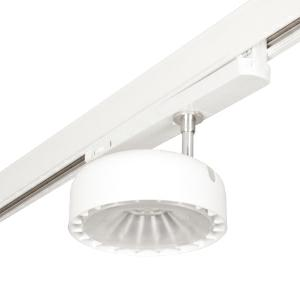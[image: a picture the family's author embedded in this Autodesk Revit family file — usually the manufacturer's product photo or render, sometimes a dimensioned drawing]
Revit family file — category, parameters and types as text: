
# Revit family: 3f_filippi_-_3f_emilio_track_ellittico_3f_filippi_-_47622_-_3f_emilio_tk_led_4000-830_ell
name_source: partatom
category: Lighting Fixtures
units: mm (PartAtom-declared; Revit-internal decimal feet)

## family parameters
Cut with Voids When Loaded = No
Host = Face
Light Source = No
Part Type = Normal
Room Calculation Point = No
Round Connector Dimension = Use Diameter
Shared = No

## types (1)
- 3F Filippi - 3F Emilio Track Ellittico (1 x LED, 3927 lm, 34 W, 3000 K)
    Apparent Load = 34 VA
    Approval mark = CE
    CIE Flux Codes = 84 95 99 100 100
    Color Rendering = 80
    Color Temperature = 3000 K
    Control Gear = Electronic ballast
    Default Elevation = 1800 mm
    Description = Adjustable spot light with minimal dimensions for accent lighting, to be integrated into the busbar.

ILLUMINOTECHNICAL
Luminous efficiency 100% (DLOR 100%, ULOR 0%).
Initial luminous flux of the luminaire 3927 lm.
Symmetrical and elliptical distribution.
Tabular UGR (CIE 117 - 4H-8H; S=0.25H; 70/50/20): RUG 22.4 - 26.8.
Beam angle: 46° - 89°.
Luminous efficacy 116 lm/W.
Lifetime (L90/B20): 30000 h. (tq+25°C)
Lifetime (L80/B20): 50000 h. (tq+25°C)
Sudden decreased luminous flux after 50000 hours: 0% (C0).
Photobiological safety in compliance with IEC/TR 62778: RG1 low risk, (IEC 62471).
In compliance with IEC/EN 62722-2-1 - IEC/EN 62717 standards.

SOURCE
Compact LED module 4000/830.
Energy efficiency class (UE 2019/2020 - UE 2019/2015): E.
CIE 13.3 Colour rendering index: CRI >80 (R9 <50%).
IES TM-30 Fidelity Index: Rf = 84 Rg = 95.
CCT nominal colour temperature 3000 K.
Colour initial tolerance (MacAdam): SDCM 3.
Zhaga Book 3 compliant.

MECHANICAL
Wired unit in white polycarbonate with busbar adaptor.
Single-piece in die-cast aluminium with passive dissipation, white colour, with perimeter cooling slots on upper edge, giving a crown of light effect to the fitting.
Invisible lock for positioning the luminous flux.
Lens made from transparent methacrylate (PMMA) with glossy surface and differentiated photo-etched.
Positioning arm in galvanised brass with sphere to allow for vertical positioning at angles from 0° to 90° and horizontal positioning from 0° to 290°.
Dimensions: diameter 130 mm, length 230 mm, height 105 mm. Weight 0.825 kg.
IP20 protection degree.
Glow-wire test resistance 650°C.

ELECTRICAL
Wiring unit separate from the body, invisible and integrated into the busbar.
Halogen Free electronic wiring 230V-50/60Hz, power factor 0.95, THD <25%, constant output current, SELV, class II, 1 driver.
Power of the luminaire 34 W.
ENEC - CE.
SAFE FLICKER: PstLM=<1 and SVM=<0.4 (IEC TR 61547-1 and IEC TR 63158), to ensure a more comfortable and safe light.
Ambient temperature from 0°C to +25°C.
Temperature class T6 max 85°C.
Relative humidity UR: <85%.

INSTALLATION
Track.

APPLICATIONS
Transit areas, spotlighting in commercial environments, exhibition areas, restaurants, shops and shop windows.

WARNING
Luminaire designed for disposal/recycling at end-of-life.
Replaceable (LED only) light source by a professional. Replaceable control gear by a professional.
    Height = 105 mm
    Lamp = 1 x LED
    Lamp Light Flux = 3927 lm
    Lamp Power = 34 W
    Lamp count = 1
    Length = 230 mm
    Lifetime = 50000 h
    Luminous efficacy = 116 lm/W
    Manufacturer = 3F Filippi
    ModVariant = No
    Model = 3F Filippi - 47622 - 3F Emilio TK LED 4000-830 ELL
    Mounting Place = Ceiling
    Mounting Type = Rail mounted
    Number of Poles = 1
    OnlyDefault = Yes
    Power Factor = 1
    Product Name = 3F Filippi - 3F Emilio Track Ellittico
    Product group = track mounted spotlight
    ProductGroupID = 12
    Protection Class = Protection class II
    Protection Degree = IP 20
    RLX_Detail_Level = 1
    RLX_Emergency_Light_Flux = 0 lm
    RLX_Emergency_Type = 0
    RLX_Emergency_Type_DB = No
    RlxData = <blob elided: 152337 chars, md5=ca9f1d0e>
    Socket = socket
    Standby Power = 0 W
    System Light Flux = 3927 lm
    System Power = 34 W
    Type Comments = Product without accessories
    Type Image = 3ffilippi_47622.jpg
    URL = http://relux.com
    VarID = ---
    Voltage = 0 V
    Weight = 0.00 kg
    Width = 130 mm

## geometry (parser evidence)
native form markers: Blend x4, Sweep x16
no freeform markers — native parametric forms only
